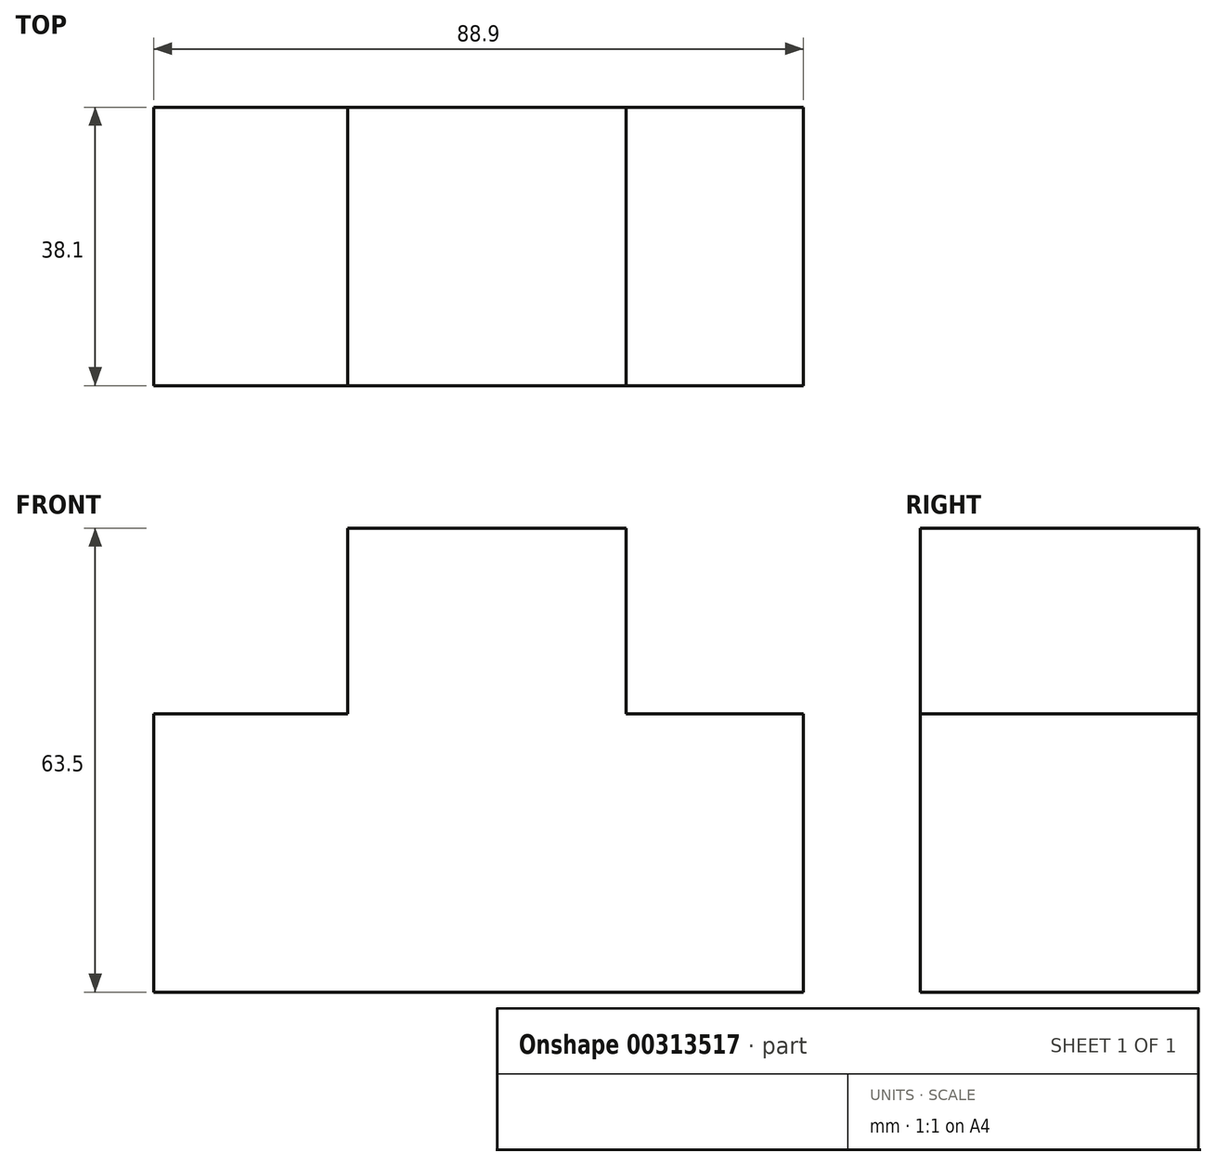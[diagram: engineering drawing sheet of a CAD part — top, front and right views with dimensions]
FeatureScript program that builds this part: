
annotation { "Feature Type Name" : "Feature", "Feature Type Description" : "" }
export const myFeature = defineFeature(function(context is Context, id is Id, definition is map)
    precondition{}
    {
        {
            var Q0;
            Q0=qCreatedBy(makeId("Front.planeOp"),FACE);
            var sketch = newSketch(context, id + "F0", { "sketchPlane" : qUnion([Q0])});
            skLineSegment(sketch, "E0", {"start": v(-42.91, 12.69) * mm, "end": v(-42.91, -25.41) * mm});
            skLineSegment(sketch, "E1", {"start": v(-42.91, -25.41) * mm, "end": v(45.99, -25.41) * mm});
            skLineSegment(sketch, "E2", {"start": v(45.99, -25.41) * mm, "end": v(45.99, 12.69) * mm});
            skLineSegment(sketch, "E3", {"start": v(45.99, 12.69) * mm, "end": v(21.74, 12.69) * mm});
            skLineSegment(sketch, "E4", {"start": v(21.74, 12.69) * mm, "end": v(21.74, 38.09) * mm});
            skLineSegment(sketch, "E5", {"start": v(21.74, 38.09) * mm, "end": v(-16.36, 38.09) * mm});
            skLineSegment(sketch, "E6", {"start": v(-16.36, 38.09) * mm, "end": v(-16.36, 12.69) * mm});
            skLineSegment(sketch, "E7", {"start": v(-16.36, 12.69) * mm, "end": v(-42.91, 12.69) * mm});
            skSolve(sketch);
        }
        {
            var Q0;
            Q0=makeQuery(id+"F0.imprint","IMPRINT",FACE,{"disambiguationData":[TD([[makeQuery(id+"F0.imprint","IMPRINT",EDGE,{"derivedFrom":sQuery(id+"F0.wireOp",EDGE,"E0")}),1.0]])]});
            extrude(context, id + "F1", {"entities" : qUnion([Q0]), "depth" : 38.1 * mm});
        }
    });
